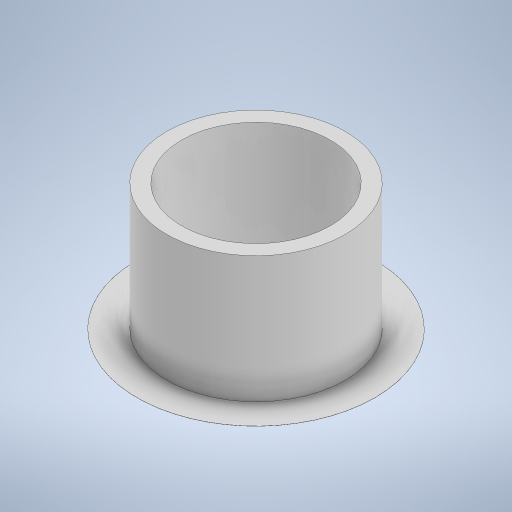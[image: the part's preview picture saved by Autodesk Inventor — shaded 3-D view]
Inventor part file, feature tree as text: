
AUTODESK INVENTOR PART (.ipt)
format: ipt  version: 2023.2 (Build 272271000, 271)  size: 239,104 bytes
history: native  units: mm
features: sketch x3, extrude x2, hole x1
ambient origin geometry x8: Origin, YZ Plane, XZ Plane, XY Plane, X Axis, Y Axis, Z Axis, Center Point
bodies: Solid1 (feature_tree)
feature tree (6):
  extrude  "Extrusion1"  Depth=0.01mm TaperAngle=0.0deg
  extrude  "Extrusion2"  Depth=8.5mm TaperAngle=0.0deg
  hole  "Hole1"  [1 undecoded]
  sketch  "Sketch1"  dims[d0=16.0mm d1=0.01mm d2=0.0mm]
  sketch  "Sketch2"  dims[d3=12.0mm d4=8.5mm d5=0.0mm]
  sketch  "Sketch3"  dims[d6=10.0mm d7=6.0mm d8=4.0mm d9=2.0mm d10=90.0deg d11=8.0mm d12=20.594885mm]
note: 1 required parameter value undecoded (feature->parameter linkage not recoverable at this tier; creation-order binding heuristic only, values carry confidence <= 0.55)
